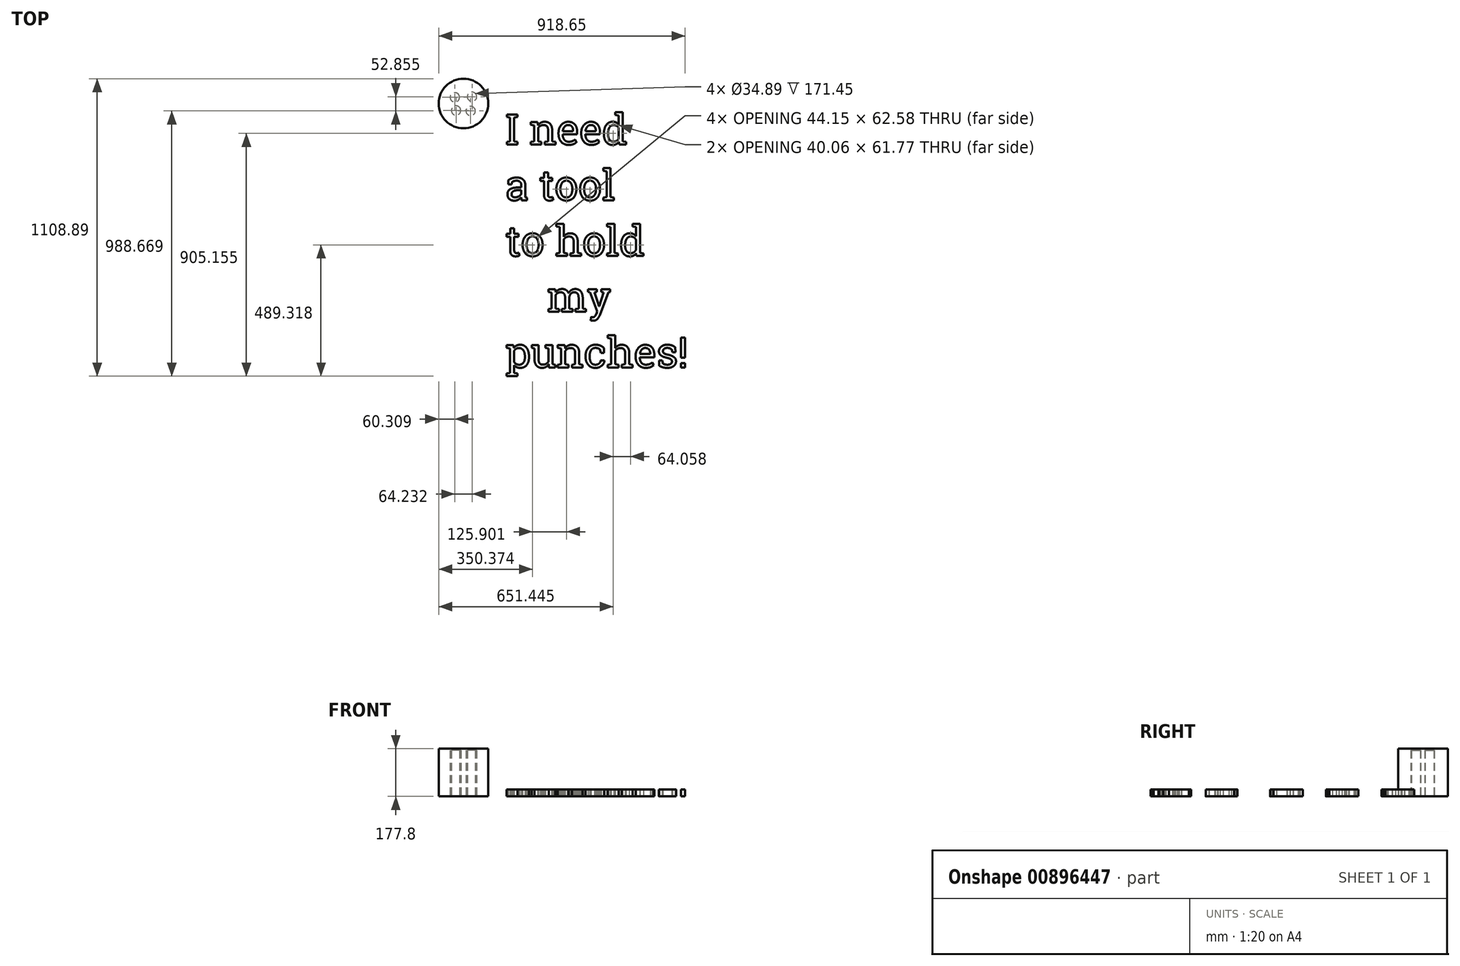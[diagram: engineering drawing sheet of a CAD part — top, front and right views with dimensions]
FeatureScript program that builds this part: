
annotation { "Feature Type Name" : "Feature", "Feature Type Description" : "" }
export const myFeature = defineFeature(function(context is Context, id is Id, definition is map)
    precondition{}
    {
        {
            var Q0;
            Q0=qCreatedBy(makeId("Top.planeOp"),FACE);
            var sketch = newSketch(context, id + "F0", { "sketchPlane" : qUnion([Q0])});
            skCircle(sketch, "E0", {"center": v(0, 0) * mm, "radius": 92.4 * mm});
            skCircle(sketch, "E1", {"center": v(-32.1, 23.23) * mm, "radius": 17.44 * mm});
            skCircle(sketch, "E2", {"center": v(32.14, 25.03) * mm, "radius": 17.44 * mm});
            skCircle(sketch, "E3", {"center": v(26.87, -27.82) * mm, "radius": 17.44 * mm});
            skCircle(sketch, "E4", {"center": v(-27.36, -26.1) * mm, "radius": 17.44 * mm});
            skCircle(sketch, "E5", {"center": v(0.66, 1.48) * mm, "radius": 39.31 * mm, "construction": true});
            skSolve(sketch);
        }
        {
            var Q0;
            Q0=makeQuery(id+"F0.imprint","IMPRINT",FACE,{"disambiguationData":[TD([[makeQuery(id+"F0.imprint","IMPRINT",EDGE,{"derivedFrom":sQuery(id+"F0.wireOp",EDGE,"E0")}),1.0]])]});
            var Q1;
            Q1=makeQuery(id+"F0.imprint","IMPRINT",FACE,{"disambiguationData":[TD([[makeQuery(id+"F0.imprint","IMPRINT",EDGE,{"derivedFrom":sQuery(id+"F0.wireOp",EDGE,"E3")}),1.0]])]});
            var Q2;
            Q2=makeQuery(id+"F0.imprint","IMPRINT",FACE,{"disambiguationData":[TD([[makeQuery(id+"F0.imprint","IMPRINT",EDGE,{"derivedFrom":sQuery(id+"F0.wireOp",EDGE,"E2")}),1.0]])]});
            var Q3;
            Q3=makeQuery(id+"F0.imprint","IMPRINT",FACE,{"disambiguationData":[TD([[makeQuery(id+"F0.imprint","IMPRINT",EDGE,{"derivedFrom":sQuery(id+"F0.wireOp",EDGE,"E1")}),1.0]])]});
            var Q4;
            Q4=makeQuery(id+"F0.imprint","IMPRINT",FACE,{"disambiguationData":[TD([[makeQuery(id+"F0.imprint","IMPRINT",EDGE,{"derivedFrom":sQuery(id+"F0.wireOp",EDGE,"E4")}),1.0]])]});
            extrude(context, id + "F1", {"entities" : qUnion([Q0, Q1, Q2, Q3, Q4]), "depth" : 177.8 * mm, "offsetDistance" : 25.4 * mm});
        }
        {
            var Q0;
            Q0=makeQuery(id+"F0.imprint","IMPRINT",FACE,{"disambiguationData":[TD([[makeQuery(id+"F0.imprint","IMPRINT",EDGE,{"derivedFrom":sQuery(id+"F0.wireOp",EDGE,"E2")}),1.0]])]});
            var Q1;
            Q1=makeQuery(id+"F0.imprint","IMPRINT",FACE,{"disambiguationData":[TD([[makeQuery(id+"F0.imprint","IMPRINT",EDGE,{"derivedFrom":sQuery(id+"F0.wireOp",EDGE,"E3")}),1.0]])]});
            var Q2;
            Q2=makeQuery(id+"F0.imprint","IMPRINT",FACE,{"disambiguationData":[TD([[makeQuery(id+"F0.imprint","IMPRINT",EDGE,{"derivedFrom":sQuery(id+"F0.wireOp",EDGE,"E4")}),1.0]])]});
            var Q3;
            Q3=makeQuery(id+"F0.imprint","IMPRINT",FACE,{"disambiguationData":[TD([[makeQuery(id+"F0.imprint","IMPRINT",EDGE,{"derivedFrom":sQuery(id+"F0.wireOp",EDGE,"E1")}),1.0]])]});
            extrude(context, id + "F2", {"entities" : qUnion([Q0, Q1, Q2, Q3]), "operationType" : NewBodyOperationType.REMOVE, "depth" : 171.45 * mm, "offsetDistance" : 25.4 * mm});
        }
        {
            var Q0;
            Q0=makeQuery(id+"F0.imprint","IMPRINT",FACE,{"disambiguationData":[TD([[makeQuery(id+"F0.imprint","IMPRINT",EDGE,{"derivedFrom":sQuery(id+"F0.wireOp",EDGE,"E0")}),1.0]])]});
            var sketch = newSketch(context, id + "F3", { "sketchPlane" : qUnion([Q0])});
            skText(sketch, "E6", { "text": "I need\na tool\nto hold\n    my\npunches!", "fontName": "RobotoSlab-Regular.ttf"});
            const initialGuessF3  = {"E6": [0.15614, -0.1529, 1, 0, 0.1134]};
            skSetInitialGuess(sketch, initialGuessF3);
            skSolve(sketch);
        }
        {
            var Q0;
            Q0 = qSketchRegion(id + "F3", true);
            extrude(context, id + "F4", {"entities" : qUnion([Q0]), "depth" : 25.4 * mm, "offsetDistance" : 25.4 * mm});
        }
    });
